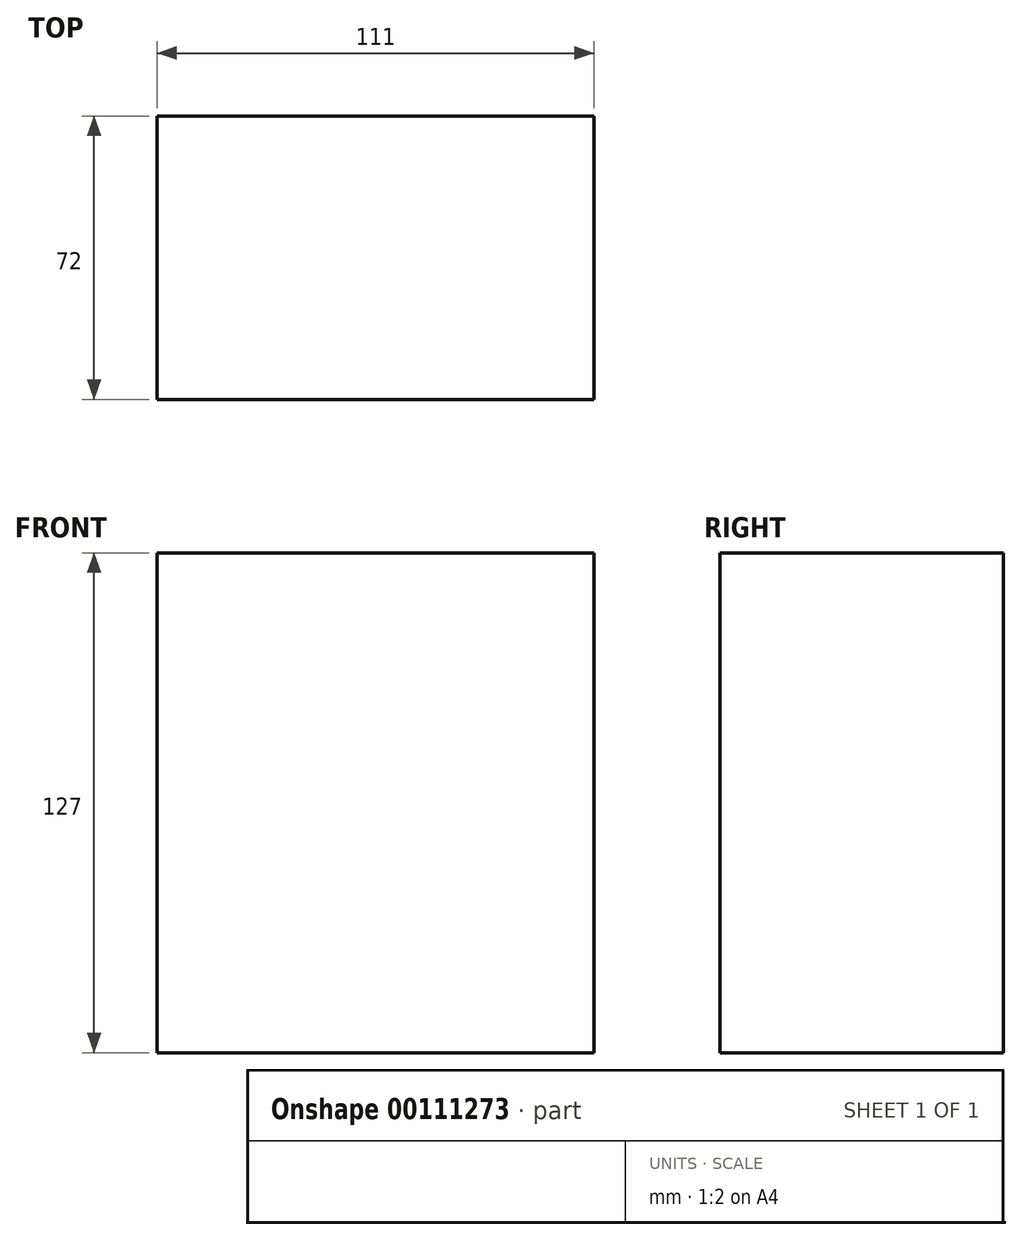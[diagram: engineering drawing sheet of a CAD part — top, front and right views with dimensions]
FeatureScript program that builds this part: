
annotation { "Feature Type Name" : "Feature", "Feature Type Description" : "" }
export const myFeature = defineFeature(function(context is Context, id is Id, definition is map)
    precondition{}
    {
        {
            var Q0;
            Q0=qCreatedBy(makeId("Top.planeOp"),FACE);
            var sketch = newSketch(context, id + "F0", { "sketchPlane" : qUnion([Q0])});
            skLineSegment(sketch, "E0.bottom", {"start": v(-55.5, 36) * mm, "end": v(55.5, 36) * mm});
            skLineSegment(sketch, "E0.top", {"start": v(-55.5, -36) * mm, "end": v(55.5, -36) * mm});
            skLineSegment(sketch, "E0.left", {"start": v(-55.5, 36) * mm, "end": v(-55.5, -36) * mm});
            skLineSegment(sketch, "E0.right", {"start": v(55.5, 36) * mm, "end": v(55.5, -36) * mm});
            skSolve(sketch);
        }
        {
            var Q0;
            Q0=makeQuery(id+"F0.imprint","IMPRINT",FACE,{"disambiguationData":[TD([[makeQuery(id+"F0.imprint","IMPRINT",EDGE,{"derivedFrom":sQuery(id+"F0.wireOp",EDGE,"E0.bottom")}),-1.0]])]});
            extrude(context, id + "F1", {"entities" : qUnion([Q0]), "depth" : 127 * mm});
        }
    });
